# Revit family: 276181xx0--Neo Daiquiri 1400x700 Superslim acrylic shower tray with waste kit - Neo Daiquiri - Roca - 276181xx0
name_source: partatom
category: Plumbing Fixtures
units: mm (PartAtom-declared; Revit-internal decimal feet)

## family parameters
Cut with Voids When Loaded = No
Host = Face
OmniClass Number = 23.65.00.00
OmniClass Title = Supply and Distribution of Liquids and Gases
Part Type = Normal
Room Calculation Point = No
Round Connector Dimension = Use Diameter
Shared = No

## types (1)
- White - Neo Daiquiri - Roca
    Antislip type = Added
    BIMobject category = Shower trays
    Default Elevation = 0 mm  [stored 0 ft]
    Depth = 1400.00
    Description = Superslim acrylic shower tray with waste kit
    Drain diameter (mm) = 90 mm  [stored 0.295276 ft]
    Eco green certification = No
    Edition number = 0
    Height = 40 mm  [stored 0.131234 ft]
    IFC Classification = Furnishing Element
    Installation instructions = http://www.roca.com
    Length = 1400 mm  [stored 4.59318 ft]
    Manufacturer name = Roca
    Manufacturer url = http://www.roca.com
    Material = White - Neo Daiquiri - Roca
    Model = 276181..0
    NBS Reference Code = 35-06-84
    NBS Reference Description = Shower Trays
    Nominal height = 40.00
    Nominal width = 700.00
    Outlet Diameter = 90 mm  [stored 0.295276 ft]
    Product Guid = d054fcd9-fae2-41fc-b370-bf8fa0a46dcd
    Product SKU = A276181000
    Product data url = http://roca.bimobject.com
    Product family = Neo Daiquiri
    Product group = SHOWER TRAYS
    QR code = https://www.roca.com
    Shape = Rectangular
Shape: Rectangular
    Suitable for Children = No
    Suitable for Handicapped = No
    UNSPSC Code = 301815
    UNSPSC Name = Sanitary ware
    URL = http://www.roca.com
    Uniclass 1.4 Code = L72143
    Uniclass 1.4 Description = Shower trays
    Uniclass 2.0 Code = PR-35-06-84
    Uniclass 2.0 Description = Shower Trays
    Weight Net (Kg) = 0
    Width = 700 mm  [stored 2.29659 ft]

note: [stored X ft] marks values corroborated as IEEE doubles in the binary element streams (Revit-internal decimal feet)

## geometry (parser evidence)
native form markers: Blend x2, Sweep x3
no freeform markers — native parametric forms only
